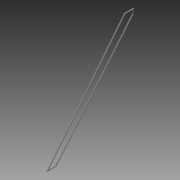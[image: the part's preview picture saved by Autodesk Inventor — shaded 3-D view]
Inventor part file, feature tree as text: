
AUTODESK INVENTOR PART (.ipt)
format: ipt  version: 2015 SP1 (Build 190203100, 203)  size: 78,848 bytes
history: native  units: in
note: dims shown in document units (in); Inventor stores cm internally (conversion verified against a paired STEP export)
features: sketch x2, sweep x1
ambient origin geometry x8: Origin, YZ Plane, XZ Plane, XY Plane, X Axis, Y Axis, Z Axis, Center Point
bodies: Solid1 (feature_tree)
feature tree (3):
  sweep  "Sweep1"
  sketch  "Sketch1"  dims[d0=0.0in d1=0.0in]
  sketch  "Sketch2"  dims[d2=1.0in d3=0.0in d4=1.0in d5=0.5in d6=0.125in d7=0.0in d8=0.0in]
